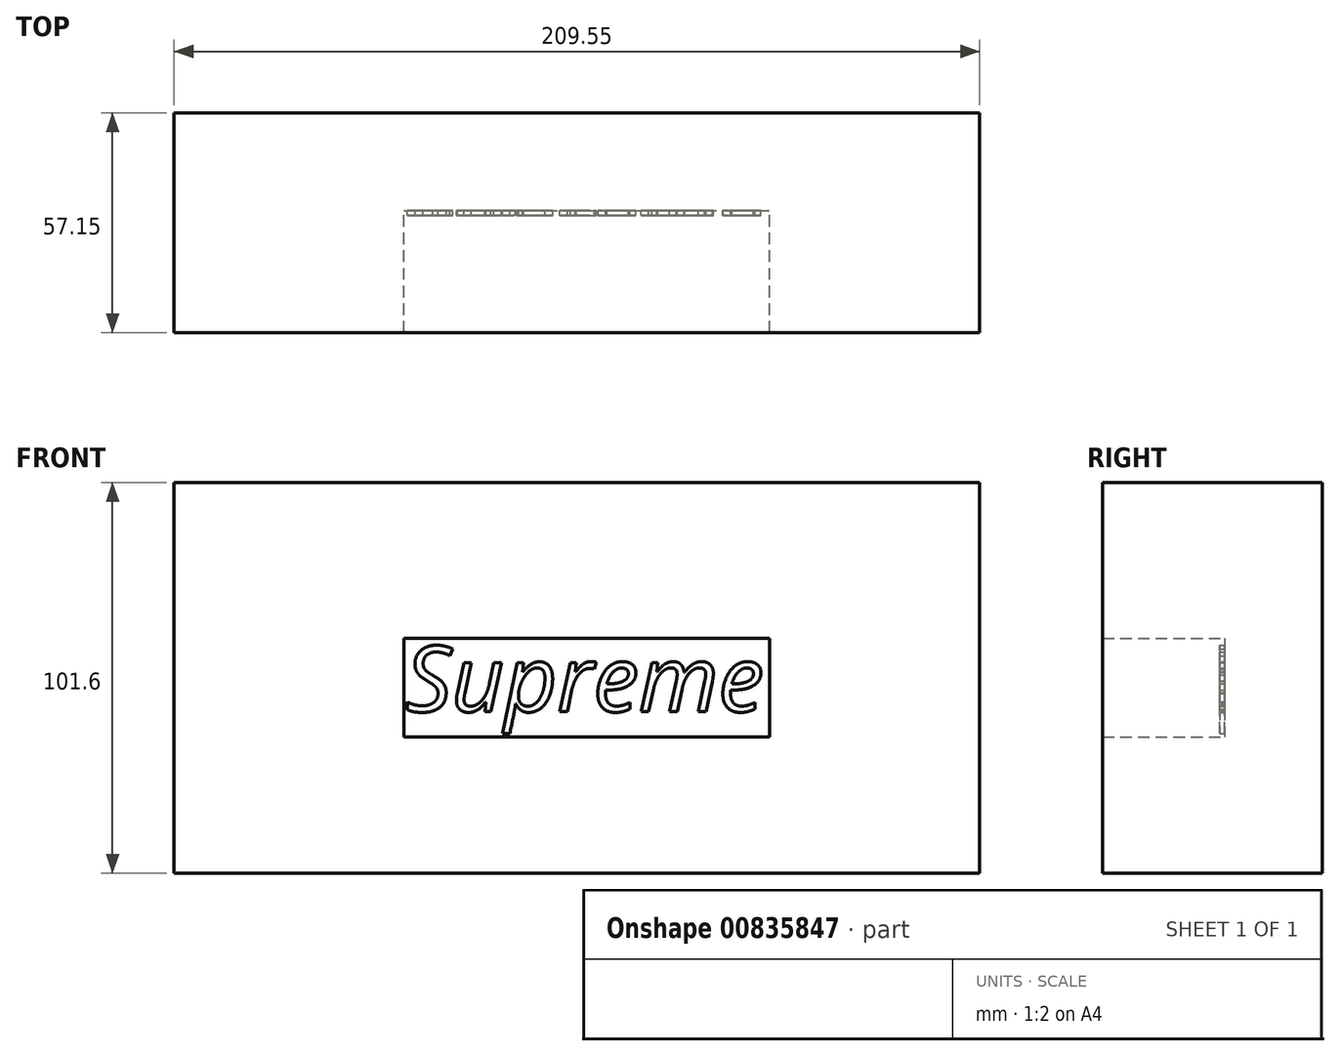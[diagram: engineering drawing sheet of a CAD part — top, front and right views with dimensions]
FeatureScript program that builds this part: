
annotation { "Feature Type Name" : "Feature", "Feature Type Description" : "" }
export const myFeature = defineFeature(function(context is Context, id is Id, definition is map)
    precondition{}
    {
        {
            var Q0;
            Q0=qCreatedBy(makeId("Front.planeOp"),FACE);
            var sketch = newSketch(context, id + "F0", { "sketchPlane" : qUnion([Q0])});
            skLineSegment(sketch, "E0.bottom", {"start": v(-97.1, 52.87) * mm, "end": v(112.45, 52.87) * mm});
            skLineSegment(sketch, "E0.top", {"start": v(-97.1, -48.73) * mm, "end": v(112.45, -48.73) * mm});
            skLineSegment(sketch, "E0.left", {"start": v(-97.1, 52.87) * mm, "end": v(-97.1, -48.73) * mm});
            skLineSegment(sketch, "E0.right", {"start": v(112.45, 52.87) * mm, "end": v(112.45, -48.73) * mm});
            skSolve(sketch);
        }
        {
            var Q0;
            Q0=makeQuery(id+"F0.imprint","IMPRINT",FACE,{"disambiguationData":[TD([[makeQuery(id+"F0.imprint","IMPRINT",EDGE,{"derivedFrom":sQuery(id+"F0.wireOp",EDGE,"E0.bottom")}),-1.0]])]});
            extrude(context, id + "F1", {"entities" : qUnion([Q0]), "depth" : 57.15 * mm, "offsetDistance" : 25.4 * mm});
        }
        {
            var Q0;
            Q0=qCreatedBy(makeId("Front.planeOp"),FACE);
            cPlane(context, id + "F2", {"entities" : qUnion([Q0]), "cplaneType" : CPlaneType.OFFSET, "offset" : 25.4 * mm, "width" : 152.4 * mm, "height" : 152.4 * mm});
        }
        {
            var Q0;
            Q0=qCreatedBy(id+"F2.planeOp",FACE);
            var sketch = newSketch(context, id + "F3", { "sketchPlane" : qUnion([Q0])});
            skLineSegment(sketch, "E1.bottom", {"start": v(-37.28, 12.37) * mm, "end": v(57.86, 12.37) * mm});
            skLineSegment(sketch, "E1.top", {"start": v(-37.28, -13.24) * mm, "end": v(57.86, -13.24) * mm});
            skLineSegment(sketch, "E1.left", {"start": v(-37.28, 12.37) * mm, "end": v(-37.28, -13.24) * mm});
            skLineSegment(sketch, "E1.right", {"start": v(57.86, 12.37) * mm, "end": v(57.86, -13.24) * mm});
            skSolve(sketch);
        }
        {
            var Q0;
            Q0=makeQuery(id+"F3.imprint","IMPRINT",FACE,{"disambiguationData":[TD([[makeQuery(id+"F3.imprint","IMPRINT",EDGE,{"derivedFrom":sQuery(id+"F3.wireOp",EDGE,"E1.bottom")}),-1.0]])]});
            extrude(context, id + "F4", {"entities" : qUnion([Q0]), "operationType" : NewBodyOperationType.REMOVE, "depth" : 57.15 * mm, "offsetDistance" : 25.4 * mm});
        }
        {
            var Q0;
            Q0=qCreatedBy(id+"F2.planeOp",FACE);
            var sketch = newSketch(context, id + "F5", { "sketchPlane" : qUnion([Q0])});
            skText(sketch, "E2", { "text": "Supreme", "fontName": "OpenSans-Italic.ttf"});
            const initialGuessF5  = {"E2": [-0.03694, -0.00668, 1, 0, 0.01716]};
            skSetInitialGuess(sketch, initialGuessF5);
            skSolve(sketch);
        }
        {
            var Q0;
            Q0 = qSketchRegion(id + "F5", true);
            extrude(context, id + "F6", {"entities" : qUnion([Q0]), "operationType" : NewBodyOperationType.ADD, "depth" : 1.27 * mm, "offsetDistance" : 25.4 * mm});
        }
    });
